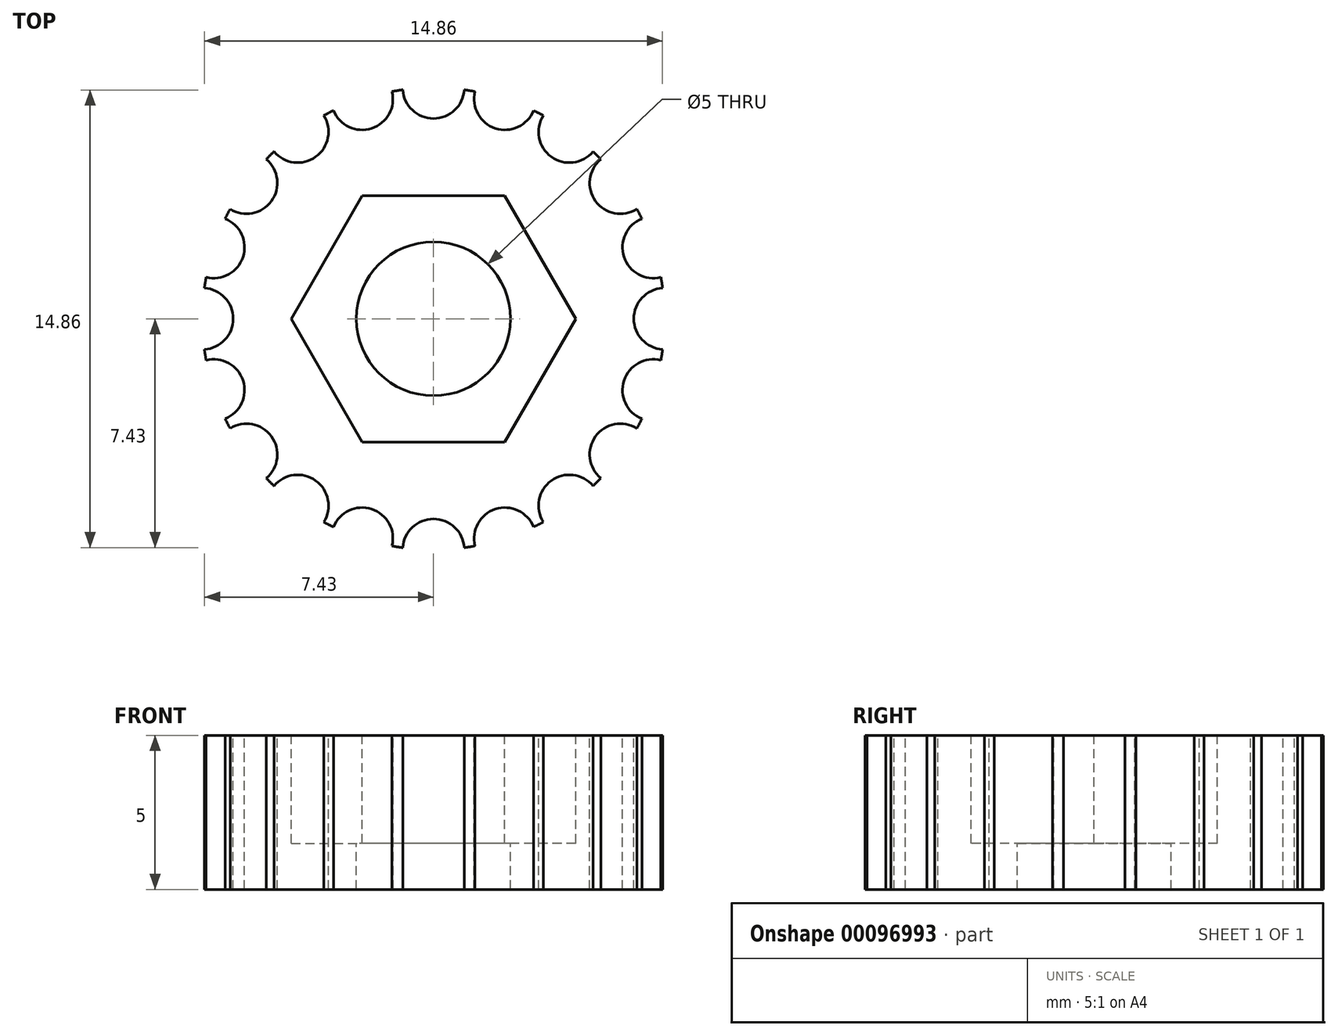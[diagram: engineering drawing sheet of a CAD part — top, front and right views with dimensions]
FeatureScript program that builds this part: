
annotation { "Feature Type Name" : "Feature", "Feature Type Description" : "" }
export const myFeature = defineFeature(function(context is Context, id is Id, definition is map)
    precondition{}
    {
        {
            var Q0;
            Q0=qCreatedBy(makeId("Top.planeOp"),FACE);
            var sketch = newSketch(context, id + "F0", { "sketchPlane" : qUnion([Q0])});
            skCircle(sketch, "E0", {"center": v(0, 0) * mm, "radius": 7.5 * mm});
            skSolve(sketch);
        }
        {
            var Q0;
            Q0 = qSketchRegion(id + "F0", true);
            extrude(context, id + "F1", {"entities" : qUnion([Q0]), "depth" : 5 * mm});
        }
        {
            var Q0;
            Q0=makeQuery(id+"F1.opExtrude","CAP_FACE",FACE,{"disambiguationData":[OSD([sQuery(id+"F0.wireOp",EDGE,"E0")])],"isStart":false});
            var sketch = newSketch(context, id + "F2", { "sketchPlane" : qUnion([Q0])});
            skPoint(sketch, "E1.0.midPoint", {"position": v(3.46, -2) * mm});
            skCircle(sketch, "E2", {"center": v(0, 7.5) * mm, "radius": 1 * mm});
            skCircle(sketch, "E3", {"center": v(0, 0) * mm, "radius": 2.5 * mm});
            skCircle(sketch, "E4.1.0", {"center": v(-2.32, 7.13) * mm, "radius": 1 * mm});
            skCircle(sketch, "E4.2.0", {"center": v(-4.4, 6.07) * mm, "radius": 1 * mm});
            skCircle(sketch, "E4.3.0", {"center": v(-6.07, 4.4) * mm, "radius": 1 * mm});
            skCircle(sketch, "E4.4.0", {"center": v(-7.13, 2.32) * mm, "radius": 1 * mm});
            skCircle(sketch, "E4.5.0", {"center": v(-7.5, 0) * mm, "radius": 1 * mm});
            skCircle(sketch, "E4.6.0", {"center": v(-7.13, -2.32) * mm, "radius": 1 * mm});
            skCircle(sketch, "E4.7.0", {"center": v(-6.07, -4.4) * mm, "radius": 1 * mm});
            skCircle(sketch, "E4.8.0", {"center": v(-4.4, -6.07) * mm, "radius": 1 * mm});
            skCircle(sketch, "E4.9.0", {"center": v(-2.32, -7.13) * mm, "radius": 1 * mm});
            skCircle(sketch, "E4.10.0", {"center": v(0, -7.5) * mm, "radius": 1 * mm});
            skCircle(sketch, "E4.11.0", {"center": v(2.32, -7.13) * mm, "radius": 1 * mm});
            skCircle(sketch, "E4.12.0", {"center": v(4.4, -6.07) * mm, "radius": 1 * mm});
            skCircle(sketch, "E4.13.0", {"center": v(6.07, -4.4) * mm, "radius": 1 * mm});
            skCircle(sketch, "E4.14.0", {"center": v(7.13, -2.32) * mm, "radius": 1 * mm});
            skCircle(sketch, "E4.15.0", {"center": v(7.5, 0) * mm, "radius": 1 * mm});
            skCircle(sketch, "E4.16.0", {"center": v(7.13, 2.32) * mm, "radius": 1 * mm});
            skCircle(sketch, "E4.17.0", {"center": v(6.07, 4.4) * mm, "radius": 1 * mm});
            skCircle(sketch, "E4.18.0", {"center": v(4.4, 6.07) * mm, "radius": 1 * mm});
            skCircle(sketch, "E4.19.0", {"center": v(2.32, 7.13) * mm, "radius": 1 * mm});
            skSolve(sketch);
        }
        {
            var Q0;
            Q0 = qSketchRegion(id + "F2", true);
            extrude(context, id + "F3", {"entities" : qUnion([Q0]), "operationType" : NewBodyOperationType.REMOVE, "oppositeDirection" : true, "depth" : 25 * mm});
        }
        {
            var Q0;
            Q0=makeQuery(id+"F1.opExtrude","CAP_FACE",FACE,{"disambiguationData":[OSD([sQuery(id+"F0.wireOp",EDGE,"E0")])],"isStart":false});
            var sketch = newSketch(context, id + "F4", { "sketchPlane" : qUnion([Q0])});
            skCircle(sketch, "E5.cCircle", {"center": v(0, 0) * mm, "radius": 4 * mm, "construction": true});
            skLineSegment(sketch, "E5.0", {"start": v(2.3, -4) * mm, "end": v(-2.3, -4) * mm});
            skLineSegment(sketch, "E5.1", {"start": v(-2.3, -4) * mm, "end": v(-4.62, 0) * mm});
            skLineSegment(sketch, "E5.2", {"start": v(-4.62, 0) * mm, "end": v(-2.3, 4) * mm});
            skLineSegment(sketch, "E5.3", {"start": v(-2.3, 4) * mm, "end": v(2.3, 4) * mm});
            skLineSegment(sketch, "E5.4", {"start": v(2.3, 4) * mm, "end": v(4.62, 0) * mm});
            skLineSegment(sketch, "E5.5", {"start": v(4.62, 0) * mm, "end": v(2.3, -4) * mm});
            skPoint(sketch, "E5.0.midPoint", {"position": v(0, -4) * mm});
            skSolve(sketch);
        }
        {
            var Q0;
            Q0 = qSketchRegion(id + "F4", true);
            extrude(context, id + "F5", {"entities" : qUnion([Q0]), "operationType" : NewBodyOperationType.REMOVE, "oppositeDirection" : true, "depth" : 3.5 * mm});
        }
    });
